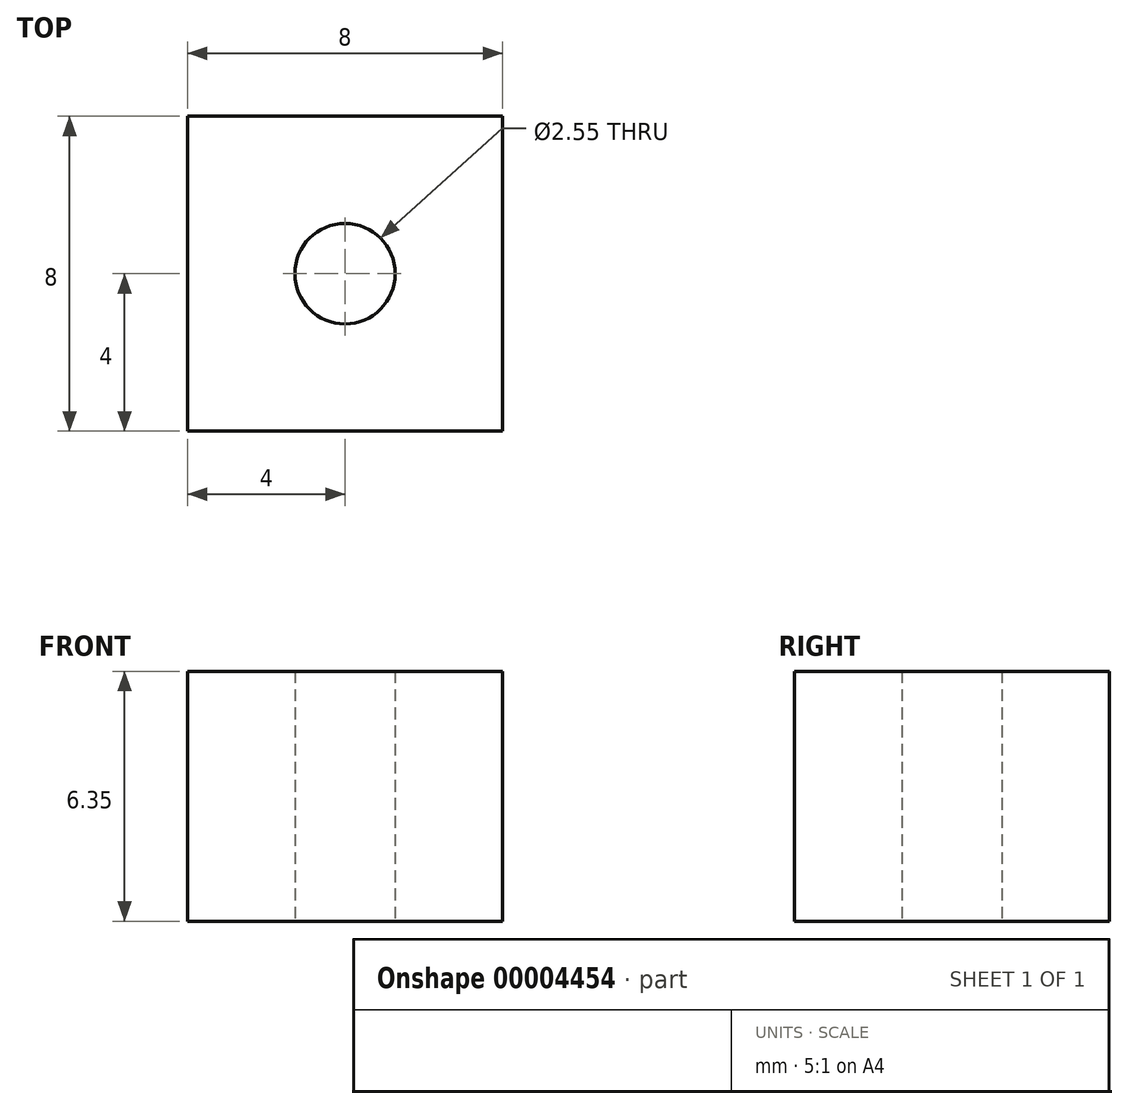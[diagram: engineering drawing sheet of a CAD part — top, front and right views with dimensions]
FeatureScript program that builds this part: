
annotation { "Feature Type Name" : "Feature", "Feature Type Description" : "" }
export const myFeature = defineFeature(function(context is Context, id is Id, definition is map)
    precondition{}
    {
        {
            var Q0;
            Q0=qCreatedBy(makeId("Top.planeOp"),FACE);
            var sketch = newSketch(context, id + "F0", { "sketchPlane" : qUnion([Q0])});
            skCircle(sketch, "E0", {"center": v(0, 0) * mm, "radius": 1.28 * mm});
            skLineSegment(sketch, "E1.rect.bottom", {"start": v(4, 4) * mm, "end": v(-4, 4) * mm});
            skLineSegment(sketch, "E1.rect.top", {"start": v(4, -4) * mm, "end": v(-4, -4) * mm});
            skLineSegment(sketch, "E1.rect.left", {"start": v(4, 4) * mm, "end": v(4, -4) * mm});
            skLineSegment(sketch, "E1.rect.right", {"start": v(-4, 4) * mm, "end": v(-4, -4) * mm});
            skSolve(sketch);
        }
        {
            var Q0;
            Q0=makeQuery(id+"F0.imprint","IMPRINT",FACE,{"disambiguationData":[TD([[makeQuery(id+"F0.imprint","IMPRINT",EDGE,{"derivedFrom":sQuery(id+"F0.wireOp",EDGE,"E0")}),-1.0]])]});
            extrude(context, id + "F1", {"entities" : qUnion([Q0]), "depth" : 6.35 * mm});
        }
    });
